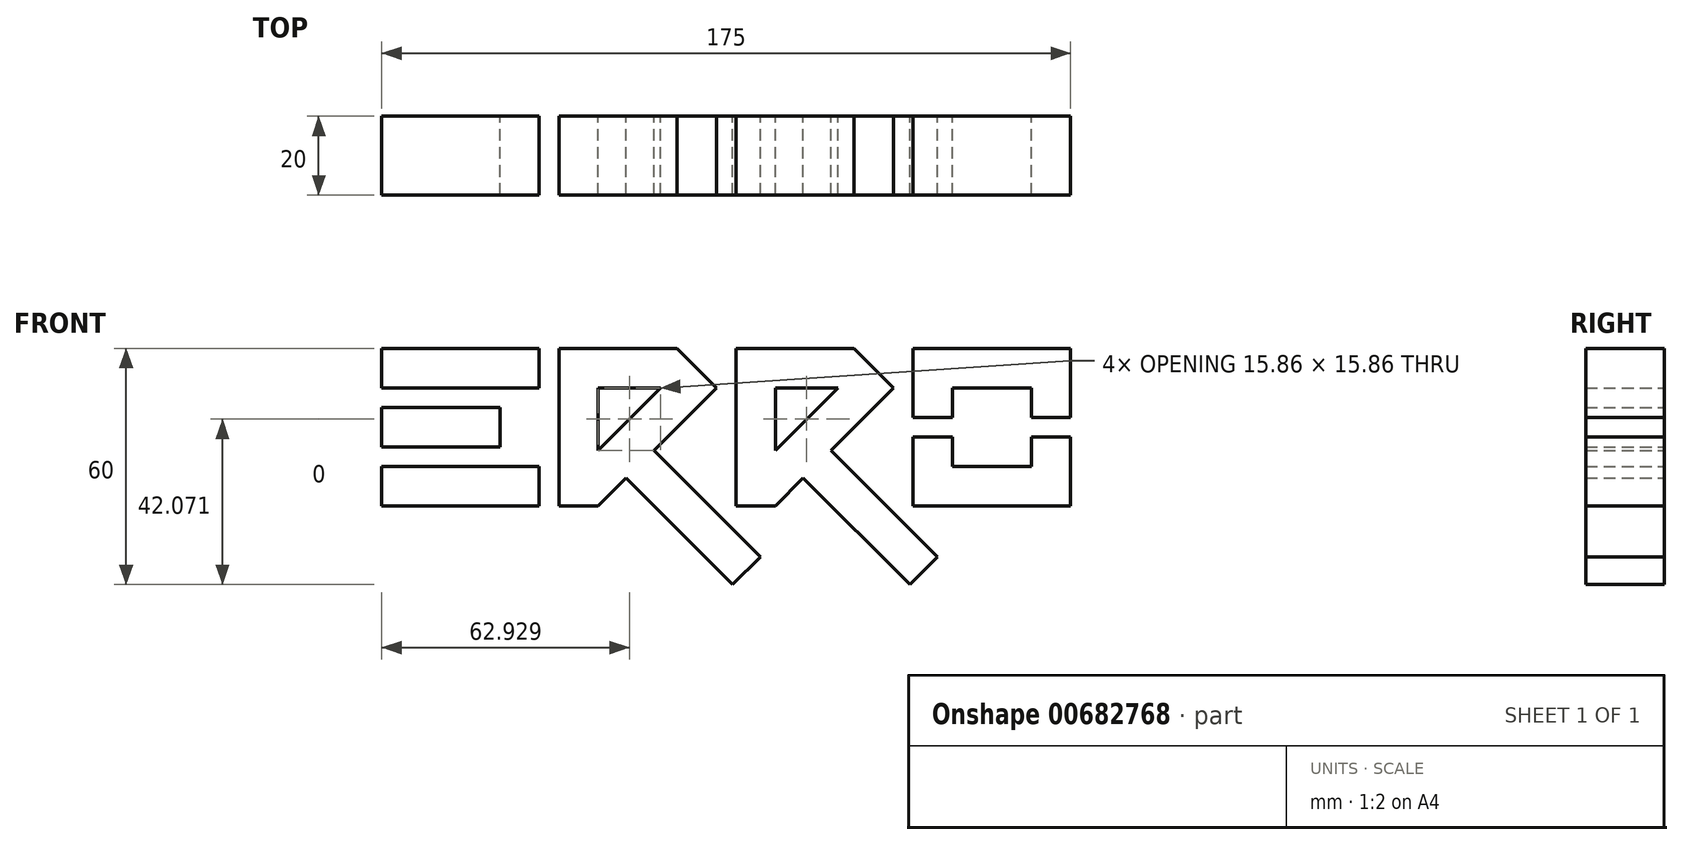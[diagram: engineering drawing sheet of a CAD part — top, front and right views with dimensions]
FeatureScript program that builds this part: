
annotation { "Feature Type Name" : "Feature", "Feature Type Description" : "" }
export const myFeature = defineFeature(function(context is Context, id is Id, definition is map)
    precondition{}
    {
        {
            var Q0;
            Q0=qCreatedBy(makeId("Front.planeOp"),FACE);
            var sketch = newSketch(context, id + "F0", { "sketchPlane" : qUnion([Q0])});
            skLineSegment(sketch, "E0.bottom", {"start": v(0, 0) * mm, "end": v(-40, 0) * mm});
            skLineSegment(sketch, "E0.top", {"start": v(0, 10) * mm, "end": v(-40, 10) * mm});
            skLineSegment(sketch, "E0.left", {"start": v(0, 0) * mm, "end": v(0, 10) * mm});
            skLineSegment(sketch, "E0.right", {"start": v(-40, 0) * mm, "end": v(-40, 10) * mm});
            skLineSegment(sketch, "E1.bottom", {"start": v(-40, 25) * mm, "end": v(-10, 25) * mm});
            skLineSegment(sketch, "E1.top", {"start": v(-40, 15) * mm, "end": v(-10, 15) * mm});
            skLineSegment(sketch, "E1.left", {"start": v(-40, 25) * mm, "end": v(-40, 15) * mm});
            skLineSegment(sketch, "E1.right", {"start": v(-10, 25) * mm, "end": v(-10, 15) * mm});
            skLineSegment(sketch, "E2.bottom", {"start": v(-40, 30) * mm, "end": v(0, 30) * mm});
            skLineSegment(sketch, "E2.top", {"start": v(-40, 40) * mm, "end": v(0, 40) * mm});
            skLineSegment(sketch, "E2.left", {"start": v(-40, 30) * mm, "end": v(-40, 40) * mm});
            skLineSegment(sketch, "E2.right", {"start": v(0, 30) * mm, "end": v(0, 40) * mm});
            skLineSegment(sketch, "E3", {"start": v(5, 0) * mm, "end": v(5, 40) * mm});
            skLineSegment(sketch, "E4", {"start": v(5, 40) * mm, "end": v(35, 40) * mm});
            skLineSegment(sketch, "E5", {"start": v(45, 40) * mm, "end": v(45, 30) * mm, "construction": true});
            skLineSegment(sketch, "E6", {"start": v(15, 0) * mm, "end": v(5, 0) * mm});
            skLineSegment(sketch, "E7", {"start": v(45, 30) * mm, "end": v(29.14, 14.14) * mm});
            skLineSegment(sketch, "E8", {"start": v(15, 0) * mm, "end": v(15, 0) * mm});
            skLineSegment(sketch, "E9", {"start": v(15, 30) * mm, "end": v(30.86, 30) * mm});
            skLineSegment(sketch, "E10", {"start": v(30.86, 30) * mm, "end": v(15, 14.14) * mm});
            skLineSegment(sketch, "E11", {"start": v(15, 14.14) * mm, "end": v(15, 30) * mm});
            skLineSegment(sketch, "E12", {"start": v(22.07, 7.07) * mm, "end": v(49.14, -20) * mm});
            skLineSegment(sketch, "E13", {"start": v(56.21, -12.93) * mm, "end": v(29.14, 14.14) * mm});
            skLineSegment(sketch, "E14", {"start": v(15, 14.14) * mm, "end": v(22.07, 7.07) * mm, "construction": true});
            skLineSegment(sketch, "E15.trimOffspring", {"start": v(22.07, 7.07) * mm, "end": v(15, 0) * mm});
            skLineSegment(sketch, "E16", {"start": v(50, 0) * mm, "end": v(50, 40) * mm});
            skLineSegment(sketch, "E17", {"start": v(50, 40) * mm, "end": v(80, 40) * mm});
            skLineSegment(sketch, "E18", {"start": v(90, 40) * mm, "end": v(90, 30) * mm, "construction": true});
            skLineSegment(sketch, "E19", {"start": v(60, 0) * mm, "end": v(50, 0) * mm});
            skLineSegment(sketch, "E20", {"start": v(90, 30) * mm, "end": v(74.14, 14.14) * mm});
            skLineSegment(sketch, "E21", {"start": v(60, 30) * mm, "end": v(75.86, 30) * mm});
            skLineSegment(sketch, "E22", {"start": v(75.86, 30) * mm, "end": v(60, 14.14) * mm});
            skLineSegment(sketch, "E23", {"start": v(60, 14.14) * mm, "end": v(60, 30) * mm});
            skLineSegment(sketch, "E24", {"start": v(67.07, 7.07) * mm, "end": v(94.14, -20) * mm});
            skLineSegment(sketch, "E25", {"start": v(101.21, -12.93) * mm, "end": v(74.14, 14.14) * mm});
            skLineSegment(sketch, "E26", {"start": v(60, 14.14) * mm, "end": v(67.07, 7.07) * mm, "construction": true});
            skLineSegment(sketch, "E27.trimOffspring", {"start": v(67.07, 7.07) * mm, "end": v(60, 0) * mm});
            skLineSegment(sketch, "E28.bottom", {"start": v(95, 0) * mm, "end": v(135, 0) * mm});
            skLineSegment(sketch, "E28.top", {"start": v(95, 40) * mm, "end": v(135, 40) * mm});
            skLineSegment(sketch, "E28.left", {"start": v(95, 0) * mm, "end": v(95, 17.5) * mm});
            skLineSegment(sketch, "E28.right", {"start": v(135, 0) * mm, "end": v(135, 17.5) * mm});
            skLineSegment(sketch, "E29.bottom", {"start": v(105, 30) * mm, "end": v(125, 30) * mm});
            skLineSegment(sketch, "E29.top", {"start": v(105, 10) * mm, "end": v(125, 10) * mm});
            skLineSegment(sketch, "E29.left", {"start": v(105, 30) * mm, "end": v(105, 22.5) * mm});
            skLineSegment(sketch, "E29.right", {"start": v(125, 30) * mm, "end": v(125, 22.5) * mm});
            skLineSegment(sketch, "E30", {"start": v(95, 17.5) * mm, "end": v(105, 17.5) * mm});
            skLineSegment(sketch, "E31", {"start": v(105, 22.5) * mm, "end": v(95, 22.5) * mm});
            skLineSegment(sketch, "E32", {"start": v(125, 22.5) * mm, "end": v(135, 22.5) * mm});
            skLineSegment(sketch, "E33", {"start": v(125, 17.5) * mm, "end": v(135, 17.5) * mm});
            skLineSegment(sketch, "E34.trimOffspring", {"start": v(95, 22.5) * mm, "end": v(95, 40) * mm});
            skLineSegment(sketch, "E35.trimOffspring", {"start": v(105, 17.5) * mm, "end": v(105, 10) * mm});
            skLineSegment(sketch, "E36.trimOffspring", {"start": v(125, 17.5) * mm, "end": v(125, 10) * mm});
            skLineSegment(sketch, "E37.trimOffspring", {"start": v(135, 22.5) * mm, "end": v(135, 40) * mm});
            skLineSegment(sketch, "E38", {"start": v(49.14, -20) * mm, "end": v(56.21, -12.93) * mm});
            skLineSegment(sketch, "E39", {"start": v(94.14, -20) * mm, "end": v(101.21, -12.93) * mm});
            skLineSegment(sketch, "E40", {"start": v(45, 30) * mm, "end": v(35, 40) * mm});
            skLineSegment(sketch, "E41", {"start": v(90, 30) * mm, "end": v(80, 40) * mm});
            skSolve(sketch);
        }
        {
            var Q0;
            Q0=makeQuery(id+"F0.imprint","IMPRINT",FACE,{"disambiguationData":[TD([[makeQuery(id+"F0.imprint","IMPRINT",EDGE,{"derivedFrom":sQuery(id+"F0.wireOp",EDGE,"E2.bottom")}),1.0]])]});
            var Q1;
            Q1=makeQuery(id+"F0.imprint","IMPRINT",FACE,{"disambiguationData":[TD([[makeQuery(id+"F0.imprint","IMPRINT",EDGE,{"derivedFrom":sQuery(id+"F0.wireOp",EDGE,"E1.bottom")}),-1.0]])]});
            var Q2;
            Q2=makeQuery(id+"F0.imprint","IMPRINT",FACE,{"disambiguationData":[TD([[makeQuery(id+"F0.imprint","IMPRINT",EDGE,{"derivedFrom":sQuery(id+"F0.wireOp",EDGE,"E0.bottom")}),-1.0]])]});
            var Q3;
            Q3=makeQuery(id+"F0.imprint","IMPRINT",FACE,{"disambiguationData":[TD([[makeQuery(id+"F0.imprint","IMPRINT",EDGE,{"derivedFrom":sQuery(id+"F0.wireOp",EDGE,"E3")}),-1.0]])]});
            var Q4;
            {var subQ3=sQuery(id+"F0.wireOp",EDGE,"E17");Q4=makeQuery(id+"F0.imprint","IMPRINT",FACE,{"disambiguationData":[TD([[makeQuery(id+"F0.imprint","IMPRINT",EDGE,{"derivedFrom":subQ3}),-1.0]])]});}
            var Q5;
            Q5=makeQuery(id+"F0.imprint","IMPRINT",FACE,{"disambiguationData":[TD([[makeQuery(id+"F0.imprint","IMPRINT",EDGE,{"derivedFrom":sQuery(id+"F0.wireOp",EDGE,"E28.bottom")}),1.0]])]});
            var Q6;
            Q6=makeQuery(id+"F0.imprint","IMPRINT",FACE,{"disambiguationData":[TD([[makeQuery(id+"F0.imprint","IMPRINT",EDGE,{"derivedFrom":sQuery(id+"F0.wireOp",EDGE,"E28.top")}),-1.0]])]});
            extrude(context, id + "F1", {"entities" : qUnion([Q0, Q1, Q2, Q3, Q4, Q5, Q6]), "depth" : 20 * mm, "offsetDistance" : 25 * mm});
        }
    });
